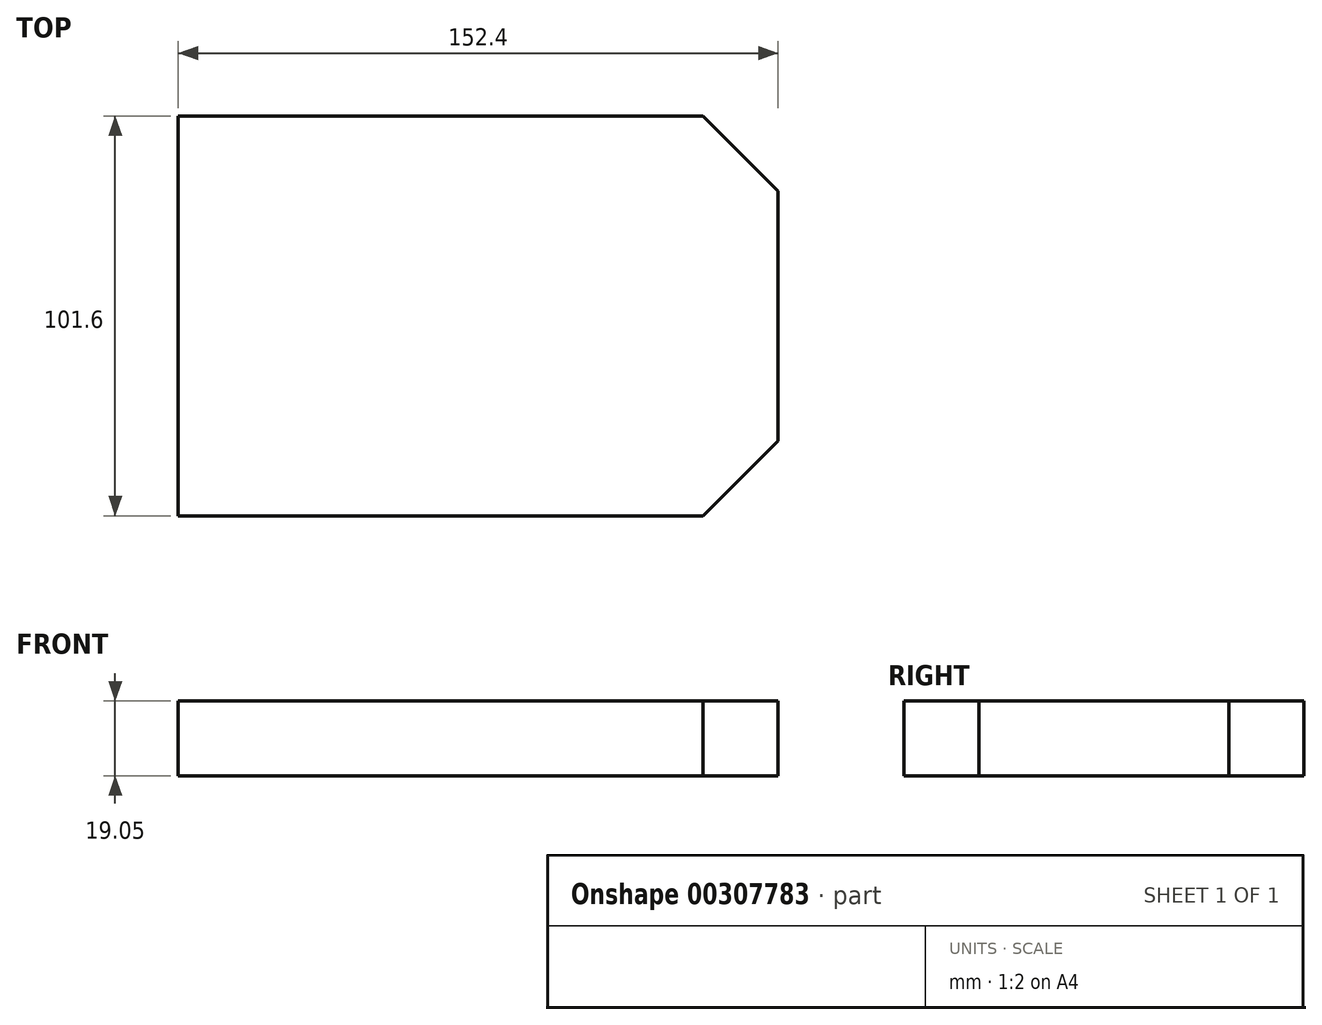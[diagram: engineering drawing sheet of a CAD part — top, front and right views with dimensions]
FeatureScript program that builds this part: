
annotation { "Feature Type Name" : "Feature", "Feature Type Description" : "" }
export const myFeature = defineFeature(function(context is Context, id is Id, definition is map)
    precondition{}
    {
        {
            var Q0;
            Q0=qCreatedBy(makeId("Top.planeOp"),FACE);
            var sketch = newSketch(context, id + "F0", { "sketchPlane" : qUnion([Q0])});
            skLineSegment(sketch, "E0.bottom", {"start": v(76.2, 50.8) * mm, "end": v(-76.2, 50.8) * mm});
            skLineSegment(sketch, "E0.top", {"start": v(76.2, -50.8) * mm, "end": v(-76.2, -50.8) * mm});
            skLineSegment(sketch, "E0.left", {"start": v(76.2, 50.8) * mm, "end": v(76.2, -50.8) * mm});
            skLineSegment(sketch, "E0.right", {"start": v(-76.2, 50.8) * mm, "end": v(-76.2, -50.8) * mm});
            skPoint(sketch, "E0.middle", {"position": v(0, 0) * mm});
            skSolve(sketch);
        }
        {
            var Q0;
            Q0 = qSketchRegion(id + "F0", true);
            extrude(context, id + "F1", {"entities" : qUnion([Q0]), "depth" : 19.05 * mm});
        }
        {
            var Q0;
            Q0=makeQuery(id+"F1.opExtrude","CAP_FACE",FACE,{"disambiguationData":[OSD([sQuery(id+"F0.wireOp",EDGE,"E0.bottom"),sQuery(id+"F0.wireOp",EDGE,"E0.top"),sQuery(id+"F0.wireOp",EDGE,"E0.left"),sQuery(id+"F0.wireOp",EDGE,"E0.right")])],"isStart":false});
            var sketch = newSketch(context, id + "F2", { "sketchPlane" : qUnion([Q0])});
            skLineSegment(sketch, "E1", {"start": v(57.15, -50.8) * mm, "end": v(76.2, -31.75) * mm});
            skLineSegment(sketch, "E2", {"start": v(76.2, 31.75) * mm, "end": v(57.15, 50.8) * mm});
            skSolve(sketch);
        }
        {
            var Q0;
            {var subQ0=sQuery(id+"F2.wireOp",EDGE,"E2");Q0=makeQuery(id+"F2.imprint","IMPRINT",FACE,{"disambiguationData":[TD([[makeQuery(id+"F2.imprint","IMPRINT",EDGE,{"derivedFrom":subQ0}),-1.0]])]});}
            var Q1;
            {var subQ0=sQuery(id+"F2.wireOp",EDGE,"E1");Q1=makeQuery(id+"F2.imprint","IMPRINT",FACE,{"disambiguationData":[TD([[makeQuery(id+"F2.imprint","IMPRINT",EDGE,{"derivedFrom":subQ0}),-1.0]])]});}
            extrude(context, id + "F3", {"entities" : qUnion([Q0, Q1]), "operationType" : NewBodyOperationType.REMOVE, "endBound" : BoundingType.THROUGH_ALL, "oppositeDirection" : true, "depth" : 25.4 * mm});
        }
    });
